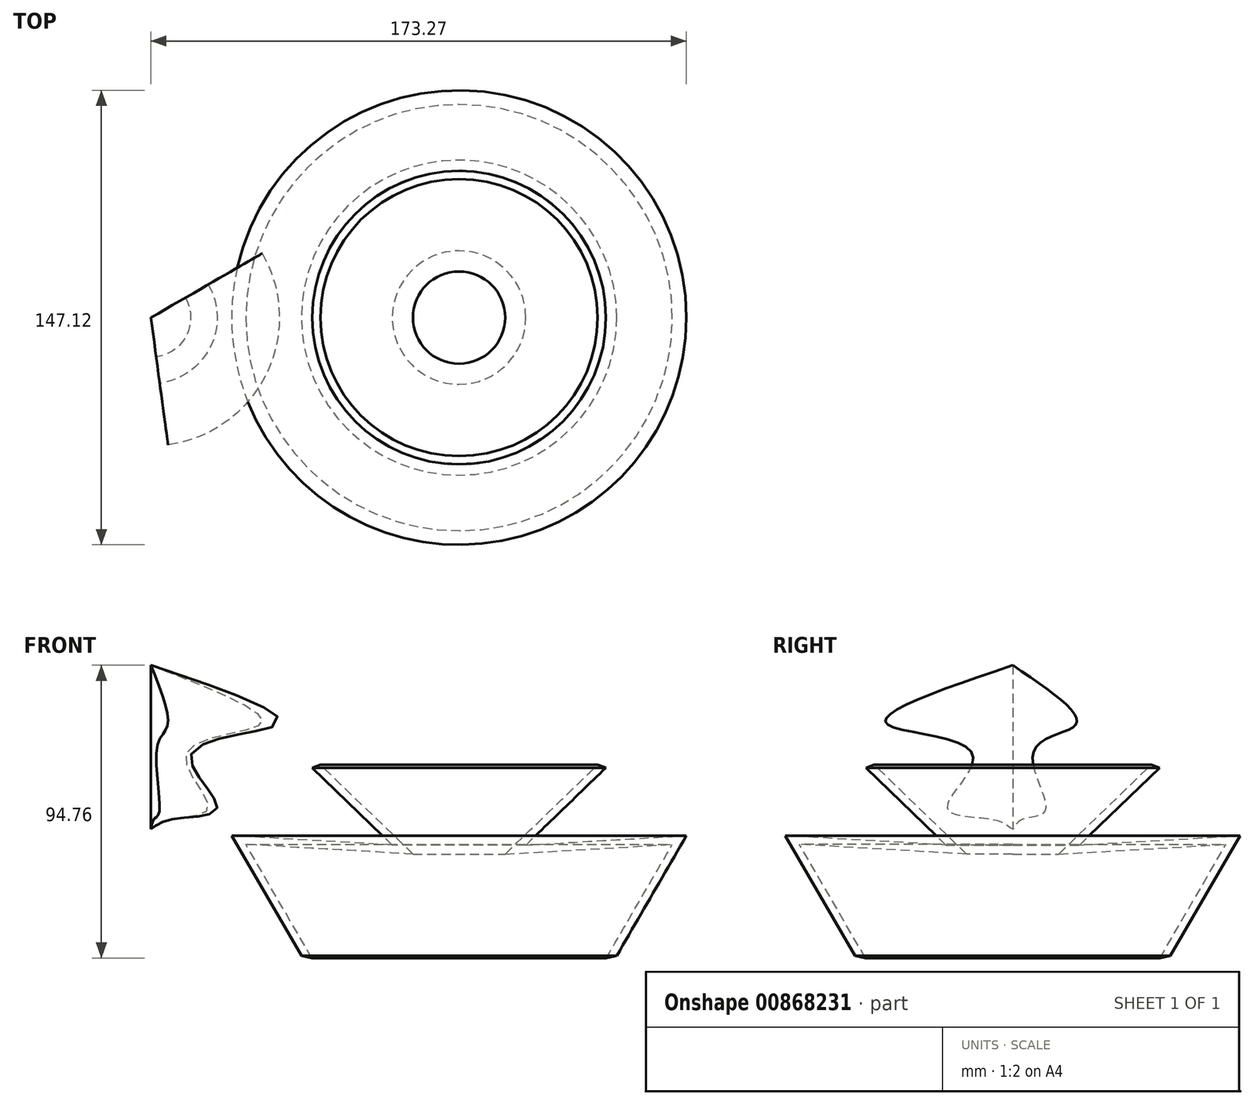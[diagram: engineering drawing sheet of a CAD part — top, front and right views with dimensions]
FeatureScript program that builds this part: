
annotation { "Feature Type Name" : "Feature", "Feature Type Description" : "" }
export const myFeature = defineFeature(function(context is Context, id is Id, definition is map)
    precondition{}
    {
        {
            var Q0;
            Q0=qCreatedBy(makeId("Front.planeOp"),FACE);
            var sketch = newSketch(context, id + "F0", { "sketchPlane" : qUnion([Q0])});
            skLineSegment(sketch, "E0", {"start": v(47.5, 51.29) * mm, "end": v(47.5, -38.01) * mm});
            skLineSegment(sketch, "E1", {"start": v(47.5, -38.01) * mm, "end": v(-3.5, -27.02) * mm});
            skLineSegment(sketch, "E2", {"start": v(-3.5, -27.02) * mm, "end": v(-26.07, 11.85) * mm});
            skLineSegment(sketch, "E3", {"start": v(-26.07, 11.85) * mm, "end": v(25.88, 8.82) * mm});
            skLineSegment(sketch, "E4", {"start": v(25.88, 8.82) * mm, "end": v(0, 33.84) * mm});
            skLineSegment(sketch, "E5", {"start": v(0, 33.84) * mm, "end": v(47.5, 51.29) * mm});
            skSolve(sketch);
        }
        {
            var Q0;
            Q0=makeQuery(id+"F0.imprint","IMPRINT",FACE,{"disambiguationData":[TD([[makeQuery(id+"F0.imprint","IMPRINT",EDGE,{"derivedFrom":sQuery(id+"F0.wireOp",EDGE,"E0")}),-1.0]])]});
            var Q1;
            Q1=sQuery(id+"F0.wireOp",EDGE,"E0");
            revolve(context, id + "F1", {"surfaceOperationType" : NewSurfaceOperationType.NEW, "entities" : qUnion([Q0]), "axis" : qUnion([Q1]), "revolveType" : RevolveType.FULL});
        }
        {
            var Q0;
            Q0=makeQuery(id+"F1.opRevolve","SWEPT_FACE",FACE,{"disambiguationData":[OSD([sQuery(id+"F0.wireOp",EDGE,"E5")])]});
            var Q1;
            Q1=makeQuery(id+"F1.opRevolve","SWEPT_FACE",FACE,{"disambiguationData":[OSD([sQuery(id+"F0.wireOp",EDGE,"E1")])]});
            shell(context, id + "F2", {"entities" : qUnion([Q0, Q1]), "thickness" : 2.54 * mm});
        }
        {
            var Q0;
            Q0=qCreatedBy(makeId("Front.planeOp"),FACE);
            var sketch = newSketch(context, id + "F3", { "sketchPlane" : qUnion([Q0])});
            skLineSegment(sketch, "E6", {"start": v(-52.2, 67.02) * mm, "end": v(-52.2, 13.94) * mm});
            skFitSpline(sketch, "E7", {"points": [v(-52.2, 67.02) * mm, v(-11.25, 47.93) * mm, v(-39.12, 38.26) * mm, v(-30.78, 21) * mm, v(-45.2, 17.21) * mm, v(-52.2, 13.94) * mm], "startDerivative": vector(235.95, -79.22) * mm, "endDerivative": vector(-41.72, -32.95) * mm});
            skSolve(sketch);
        }
        {
            var Q0;
            Q0=makeQuery(id+"F3.imprint","IMPRINT",FACE,{"disambiguationData":[TD([[makeQuery(id+"F3.imprint","IMPRINT",EDGE,{"derivedFrom":sQuery(id+"F3.wireOp",EDGE,"E6")}),1.0]])]});
            var Q1;
            Q1=sQuery(id+"F3.wireOp",EDGE,"E6");
            revolve(context, id + "F4", {"surfaceOperationType" : NewSurfaceOperationType.NEW, "entities" : qUnion([Q0]), "axis" : qUnion([Q1]), "revolveType" : RevolveType.TWO_DIRECTIONS, "angle" : 82.33 * degree, "angleBack" : 330 * degree});
        }
    });
